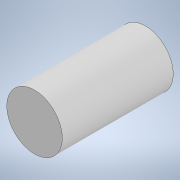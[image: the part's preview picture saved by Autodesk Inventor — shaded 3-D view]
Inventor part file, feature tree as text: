
AUTODESK INVENTOR PART (.ipt)
format: ipt  version: 2021 (Build 250183000, 183)  size: 93,184 bytes
history: native  units: mm
features: extrude x1, sketch x1
ambient origin geometry x8: Origin, YZ Plane, XZ Plane, XY Plane, X Axis, Y Axis, Z Axis, Center Point
bodies: Solid1 (feature_tree)
feature tree (2):
  extrude  "Extrusion1"  Depth=5.0mm TaperAngle=0.0deg
  sketch  "Sketch1"  dims[d0=2.5mm d1=5.0mm d2=0.0mm]
